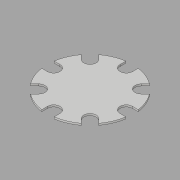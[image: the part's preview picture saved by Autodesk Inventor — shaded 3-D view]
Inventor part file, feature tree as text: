
AUTODESK INVENTOR PART (.ipt)
format: ipt  version: 2017 (Build 210142000, 142)  size: 149,504 bytes
history: native  units: in
note: dims shown in document units (in); Inventor stores cm internally (conversion verified against a paired STEP export)
features: extrude x2, sketch x2
ambient origin geometry x8: Origin, YZ Plane, XZ Plane, XY Plane, X Axis, Y Axis, Z Axis, Center Point
bodies: Solid1 (feature_tree)
feature tree (4):
  extrude  "Extrusion1"  Depth=8.0in
  extrude  "Extrusion2"  Depth=0.3937in TaperAngle=0.0deg
  sketch  "Sketch1"  dims[d0=2.75in d1=8.0in]
  sketch  "Sketch2"  dims[d2=3.1496in d4=360.0deg d6=0.3937in d7=0.0in d8=3.1496in d10=360.0deg d12=0.3937in d13=0.0in]
